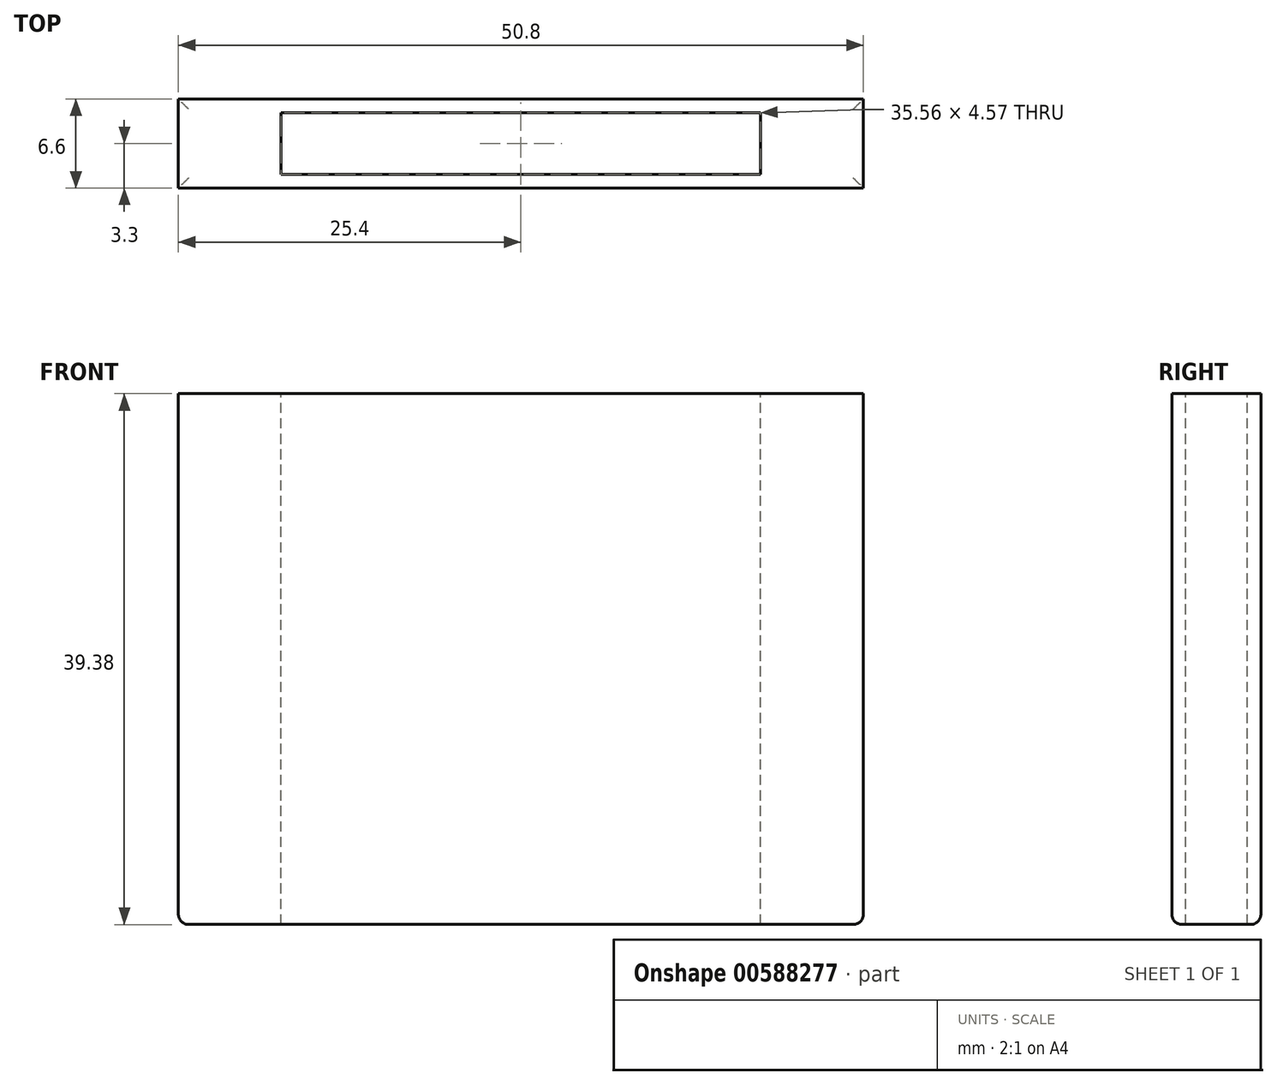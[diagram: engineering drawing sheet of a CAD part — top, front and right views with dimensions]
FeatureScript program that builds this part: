
annotation { "Feature Type Name" : "Feature", "Feature Type Description" : "" }
export const myFeature = defineFeature(function(context is Context, id is Id, definition is map)
    precondition{}
    {
        {
            var Q0;
            Q0=qCreatedBy(makeId("Front.planeOp"),FACE);
            var sketch = newSketch(context, id + "F0", { "sketchPlane" : qUnion([Q0])});
            skLineSegment(sketch, "E0.bottom", {"start": v(-25.4, 19.69) * mm, "end": v(25.4, 19.69) * mm});
            skLineSegment(sketch, "E0.top", {"start": v(-25.4, -19.68) * mm, "end": v(25.4, -19.68) * mm});
            skLineSegment(sketch, "E0.left", {"start": v(-25.4, 19.69) * mm, "end": v(-25.4, -19.68) * mm});
            skLineSegment(sketch, "E0.right", {"start": v(25.4, 19.69) * mm, "end": v(25.4, -19.68) * mm});
            skPoint(sketch, "E0.middle", {"position": v(0, 0) * mm});
            skSolve(sketch);
        }
        {
            var Q0;
            Q0=makeQuery(id+"F0.imprint","IMPRINT",FACE,{"disambiguationData":[TD([[makeQuery(id+"F0.imprint","IMPRINT",EDGE,{"derivedFrom":sQuery(id+"F0.wireOp",EDGE,"E0.bottom")}),-1.0]])]});
            extrude(context, id + "F1", {"entities" : qUnion([Q0]), "endBound" : BoundingType.SYMMETRIC, "depth" : 6.6 * mm, "offsetDistance" : 25.4 * mm});
        }
        {
            var Q0;
            Q0=makeQuery(id+"F1.opExtrude","SWEPT_FACE",FACE,{"disambiguationData":[OSD([sQuery(id+"F0.wireOp",EDGE,"E0.bottom")])]});
            var sketch = newSketch(context, id + "F2", { "sketchPlane" : qUnion([Q0])});
            skLineSegment(sketch, "E1.bottom", {"start": v(17.78, 2.29) * mm, "end": v(-17.78, 2.29) * mm});
            skLineSegment(sketch, "E1.top", {"start": v(17.78, -2.29) * mm, "end": v(-17.78, -2.29) * mm});
            skLineSegment(sketch, "E1.left", {"start": v(17.78, 2.29) * mm, "end": v(17.78, -2.29) * mm});
            skLineSegment(sketch, "E1.right", {"start": v(-17.78, 2.29) * mm, "end": v(-17.78, -2.29) * mm});
            skPoint(sketch, "E1.middle", {"position": v(0, 0) * mm});
            skSolve(sketch);
        }
        {
            var Q0;
            Q0=makeQuery(id+"F2.imprint","IMPRINT",FACE,{"disambiguationData":[TD([[makeQuery(id+"F2.imprint","IMPRINT",EDGE,{"derivedFrom":sQuery(id+"F2.wireOp",EDGE,"E1.bottom")}),1.0]])]});
            extrude(context, id + "F3", {"entities" : qUnion([Q0]), "operationType" : NewBodyOperationType.REMOVE, "oppositeDirection" : true, "depth" : 39.37 * mm, "offsetDistance" : 25.4 * mm});
        }
        {
            var Q0;
            Q0=makeQuery(id+"F1.opExtrude","CAP_EDGE",EDGE,{"disambiguationData":[OSD([sQuery(id+"F0.wireOp",EDGE,"E0.top")])],"isStart":false});
            var Q1;
            Q1=makeQuery(id+"F1.opExtrude","SWEPT_EDGE",EDGE,{"disambiguationData":[OSD([sQuery(id+"F0.wireOp",EDGE,"E0.top"),sQuery(id+"F0.wireOp",EDGE,"E0.left")])]});
            var Q2;
            Q2=makeQuery(id+"F1.opExtrude","CAP_EDGE",EDGE,{"disambiguationData":[OSD([sQuery(id+"F0.wireOp",EDGE,"E0.top")])],"isStart":true});
            var Q3;
            Q3=makeQuery(id+"F1.opExtrude","SWEPT_EDGE",EDGE,{"disambiguationData":[OSD([sQuery(id+"F0.wireOp",EDGE,"E0.top"),sQuery(id+"F0.wireOp",EDGE,"E0.right")])]});
            fillet(context, id + "F4", {"entities" : qUnion([Q0, Q1, Q2, Q3]), "radius" : 0.76 * mm, "tangentPropagation" : true, "allowEdgeOverflow" : false});
        }
    });
